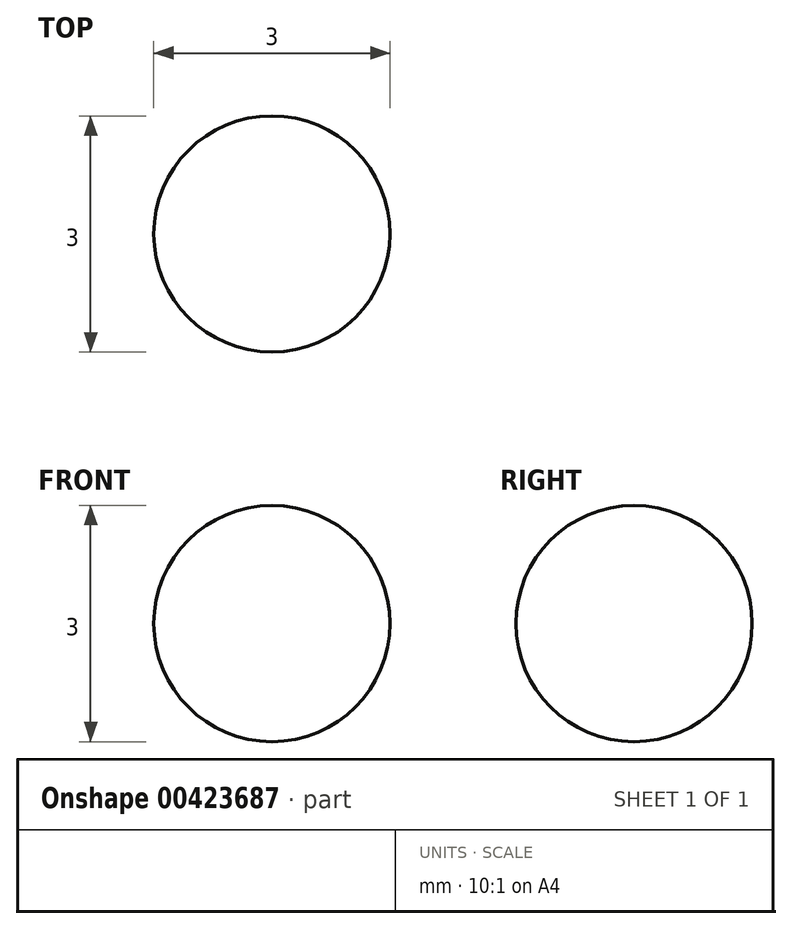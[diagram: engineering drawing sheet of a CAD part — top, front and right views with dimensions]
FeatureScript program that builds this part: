
annotation { "Feature Type Name" : "Feature", "Feature Type Description" : "" }
export const myFeature = defineFeature(function(context is Context, id is Id, definition is map)
    precondition{}
    {
        {
            var Q0;
            Q0=qCreatedBy(makeId("Right.planeOp"),FACE);
            var sketch = newSketch(context, id + "F0", { "sketchPlane" : qUnion([Q0])});
            skLineSegment(sketch, "E0", {"start": v(0, 1.5) * mm, "end": v(0, -1.5) * mm});
            skArc(sketch, "E1", {"start": v(0, -1.5) * mm, "mid": v(1.5, 0) * mm, "end": v(0, 1.5) * mm});
            skSolve(sketch);
        }
        {
            var Q0;
            Q0=makeQuery(id+"F0.imprint","IMPRINT",FACE,{"disambiguationData":[TD([[makeQuery(id+"F0.imprint","IMPRINT",EDGE,{"derivedFrom":sQuery(id+"F0.wireOp",EDGE,"E0")}),1.0]])]});
            var Q1;
            Q1=sQuery(id+"F0.wireOp",EDGE,"E0");
            revolve(context, id + "F1", {"entities" : qUnion([Q0]), "axis" : qUnion([Q1]), "revolveType" : RevolveType.FULL});
        }
    });
